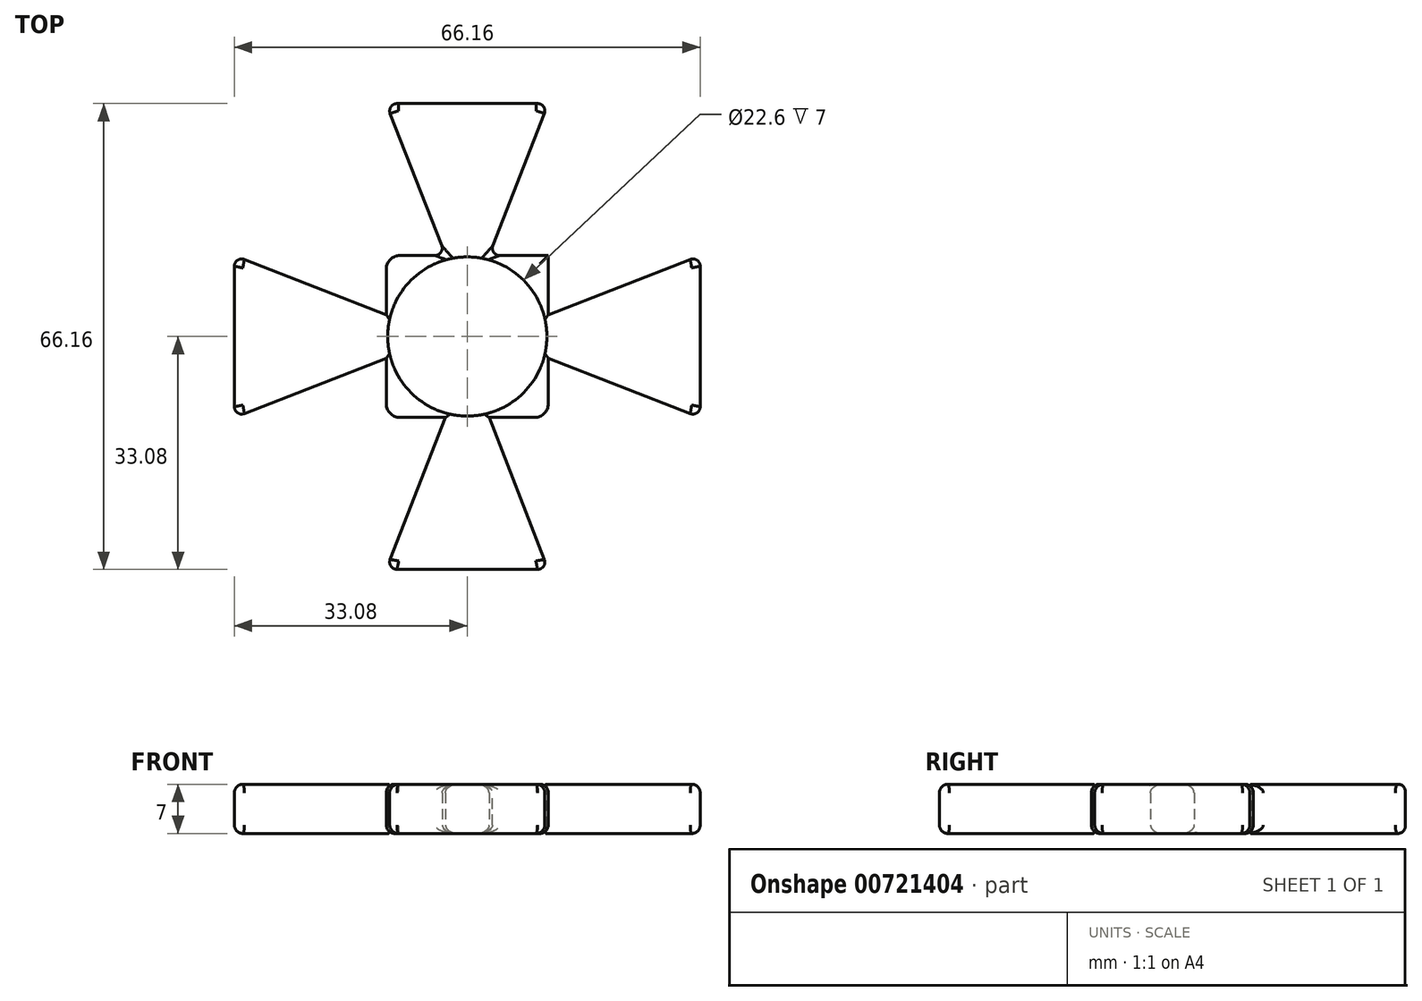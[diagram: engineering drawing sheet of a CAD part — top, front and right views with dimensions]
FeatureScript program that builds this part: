
annotation { "Feature Type Name" : "Feature", "Feature Type Description" : "" }
export const myFeature = defineFeature(function(context is Context, id is Id, definition is map)
    precondition{}
    {
        {
            var Q0;
            Q0=qCreatedBy(makeId("Top.planeOp"),FACE);
            var sketch = newSketch(context, id + "F0", { "sketchPlane" : qUnion([Q0])});
            skCircle(sketch, "E0", {"center": v(0, 0) * mm, "radius": 11.3 * mm});
            skLineSegment(sketch, "E1.bottom", {"start": v(11.5, 11.5) * mm, "end": v(-11.5, 11.5) * mm});
            skLineSegment(sketch, "E1.top", {"start": v(11.5, -11.5) * mm, "end": v(-11.5, -11.5) * mm});
            skLineSegment(sketch, "E1.left", {"start": v(11.5, 11.5) * mm, "end": v(11.5, -11.5) * mm});
            skLineSegment(sketch, "E1.right", {"start": v(-11.5, 11.5) * mm, "end": v(-11.5, -11.5) * mm});
            skLineSegment(sketch, "E2", {"start": v(-3.1, 11.5) * mm, "end": v(-11.5, 33.08) * mm});
            skLineSegment(sketch, "E3.MirrorCS", {"start": v(3.1, 11.5) * mm, "end": v(11.5, 33.08) * mm});
            skLineSegment(sketch, "E4", {"start": v(-11.5, 33.08) * mm, "end": v(11.5, 33.08) * mm});
            skLineSegment(sketch, "E5.MirrorCS", {"start": v(11.5, 33.08) * mm, "end": v(-11.5, 33.08) * mm});
            skLineSegment(sketch, "E6.MirrorCS", {"start": v(-3.1, -11.5) * mm, "end": v(-11.5, -33.08) * mm});
            skLineSegment(sketch, "E7.MirrorCS", {"start": v(3.1, -11.5) * mm, "end": v(11.5, -33.08) * mm});
            skLineSegment(sketch, "E8.MirrorCS", {"start": v(11.5, -33.08) * mm, "end": v(-11.5, -33.08) * mm});
            skLineSegment(sketch, "E9.MirrorCS", {"start": v(-11.5, 3.1) * mm, "end": v(-33.08, 11.5) * mm});
            skLineSegment(sketch, "E10.MirrorCS", {"start": v(-11.5, -3.1) * mm, "end": v(-33.08, -11.5) * mm});
            skLineSegment(sketch, "E11.MirrorCS", {"start": v(-33.08, -11.5) * mm, "end": v(-33.08, 11.5) * mm});
            skLineSegment(sketch, "E12.MirrorCS", {"start": v(11.5, 3.1) * mm, "end": v(33.08, 11.5) * mm});
            skLineSegment(sketch, "E13.MirrorCS", {"start": v(11.5, -3.1) * mm, "end": v(33.08, -11.5) * mm});
            skLineSegment(sketch, "E14.MirrorCS", {"start": v(33.08, -11.5) * mm, "end": v(33.08, 11.5) * mm});
            skSolve(sketch);
        }
        {
            var Q0;
            {var subQ0=sQuery(id+"F0.wireOp",EDGE,"E2");Q0=makeQuery(id+"F0.imprint","IMPRINT",FACE,{"disambiguationData":[TD([[makeQuery(id+"F0.imprint","IMPRINT",EDGE,{"derivedFrom":subQ0}),-1.0]])]});}
            var Q1;
            Q1=makeQuery(id+"F0.imprint","IMPRINT",FACE,{"disambiguationData":[TD([[makeQuery(id+"F0.imprint","IMPRINT",EDGE,{"derivedFrom":sQuery(id+"F0.wireOp",EDGE,"E0")}),-1.0]])]});
            var Q2;
            {var subQ0=sQuery(id+"F0.wireOp",EDGE,"E9.MirrorCS");Q2=makeQuery(id+"F0.imprint","IMPRINT",FACE,{"disambiguationData":[TD([[makeQuery(id+"F0.imprint","IMPRINT",EDGE,{"derivedFrom":subQ0}),1.0]])]});}
            var Q3;
            {var subQ0=sQuery(id+"F0.wireOp",EDGE,"E3.MirrorCS");Q3=makeQuery(id+"F0.imprint","IMPRINT",FACE,{"disambiguationData":[TD([[makeQuery(id+"F0.imprint","IMPRINT",EDGE,{"derivedFrom":subQ0}),1.0]])]});}
            var Q4;
            {var subQ0=sQuery(id+"F0.wireOp",EDGE,"E6.MirrorCS");Q4=makeQuery(id+"F0.imprint","IMPRINT",FACE,{"disambiguationData":[TD([[makeQuery(id+"F0.imprint","IMPRINT",EDGE,{"derivedFrom":subQ0}),1.0]])]});}
            var Q5;
            {var subQ0=sQuery(id+"F0.wireOp",EDGE,"E12.MirrorCS");Q5=makeQuery(id+"F0.imprint","IMPRINT",FACE,{"disambiguationData":[TD([[makeQuery(id+"F0.imprint","IMPRINT",EDGE,{"derivedFrom":subQ0}),-1.0]])]});}
            extrude(context, id + "F1", {"entities" : qUnion([Q0, Q1, Q2, Q3, Q4, Q5]), "depth" : 7 * mm, "offsetDistance" : 25 * mm});
        }
        {
            var Q0;
            Q0=makeQuery(id+"F1.opExtrude","SWEPT_EDGE",EDGE,{"disambiguationData":[OSD([sQuery(id+"F0.wireOp",EDGE,"E1.bottom"),sQuery(id+"F0.wireOp",EDGE,"E1.right")])]});
            var Q1;
            Q1=makeQuery(id+"F1.opExtrude","SWEPT_EDGE",EDGE,{"disambiguationData":[OSD([sQuery(id+"F0.wireOp",EDGE,"E1.top"),sQuery(id+"F0.wireOp",EDGE,"E1.left")])]});
            var Q2;
            Q2=makeQuery(id+"F1.opExtrude","SWEPT_EDGE",EDGE,{"disambiguationData":[OSD([sQuery(id+"F0.wireOp",EDGE,"E1.top"),sQuery(id+"F0.wireOp",EDGE,"E1.right")])]});
            fillet(context, id + "F2", {"entities" : qUnion([Q0, Q1, Q2]), "radius" : 1.93 * mm, "tangentPropagation" : true, "allowEdgeOverflow" : false});
        }
        {
            var Q0;
            {var subQ0=sQuery(id+"F0.wireOp",EDGE,"E1.right");Q0=makeQuery(id+"F1.opExtrude","CAP_EDGE",EDGE,{"disambiguationData":[OSD([subQ0]),TDD([makeQuery(id+"F0.imprint","IMPRINT",EDGE,{"disambiguationData":[TD([[makeQuery(id+"F0.imprint","INTERSECT",VERTEX,{"derivedFrom":[sQuery(id+"F0.wireOp",EDGE,"E1.bottom"),subQ0]}),-1.0]])],"derivedFrom":subQ0})])],"isStart":false});}
            var Q1;
            {var subQ0=sQuery(id+"F0.wireOp",EDGE,"E1.bottom");Q1=makeQuery(id+"F1.opExtrude","CAP_EDGE",EDGE,{"disambiguationData":[OSD([subQ0]),TDD([makeQuery(id+"F0.imprint","IMPRINT",EDGE,{"disambiguationData":[TD([[makeQuery(id+"F0.imprint","INTERSECT",VERTEX,{"derivedFrom":[subQ0,sQuery(id+"F0.wireOp",EDGE,"E1.right")]}),1.0]])],"derivedFrom":subQ0})])],"isStart":false});}
            var Q2;
            {var subQ0=sQuery(id+"F0.wireOp",EDGE,"E1.bottom");Q2=makeQuery(id+"F1.opExtrude","CAP_EDGE",EDGE,{"disambiguationData":[OSD([subQ0]),TDD([makeQuery(id+"F0.imprint","IMPRINT",EDGE,{"disambiguationData":[TD([[makeQuery(id+"F0.imprint","INTERSECT",VERTEX,{"derivedFrom":[subQ0,sQuery(id+"F0.wireOp",EDGE,"E1.left")]}),-1.0]])],"derivedFrom":subQ0})])],"isStart":false});}
            var Q3;
            {var subQ0=sQuery(id+"F0.wireOp",EDGE,"E1.left");Q3=makeQuery(id+"F1.opExtrude","CAP_EDGE",EDGE,{"disambiguationData":[OSD([subQ0]),TDD([makeQuery(id+"F0.imprint","IMPRINT",EDGE,{"disambiguationData":[TD([[makeQuery(id+"F0.imprint","INTERSECT",VERTEX,{"derivedFrom":[sQuery(id+"F0.wireOp",EDGE,"E1.bottom"),subQ0]}),-1.0]])],"derivedFrom":subQ0})])],"isStart":false});}
            var Q4;
            {var subQ0=sQuery(id+"F0.wireOp",EDGE,"E1.left");Q4=makeQuery(id+"F1.opExtrude","CAP_EDGE",EDGE,{"disambiguationData":[OSD([subQ0]),TDD([makeQuery(id+"F0.imprint","IMPRINT",EDGE,{"disambiguationData":[TD([[makeQuery(id+"F0.imprint","INTERSECT",VERTEX,{"derivedFrom":[sQuery(id+"F0.wireOp",EDGE,"E1.top"),subQ0]}),1.0]])],"derivedFrom":subQ0})])],"isStart":false});}
            var Q5;
            {var subQ0=sQuery(id+"F0.wireOp",EDGE,"E1.top");Q5=makeQuery(id+"F1.opExtrude","CAP_EDGE",EDGE,{"disambiguationData":[OSD([subQ0]),TDD([makeQuery(id+"F0.imprint","IMPRINT",EDGE,{"disambiguationData":[TD([[makeQuery(id+"F0.imprint","INTERSECT",VERTEX,{"derivedFrom":[subQ0,sQuery(id+"F0.wireOp",EDGE,"E1.left")]}),-1.0]])],"derivedFrom":subQ0})])],"isStart":false});}
            var Q6;
            {var subQ0=sQuery(id+"F0.wireOp",EDGE,"E1.left");var subQ1=sQuery(id+"F0.wireOp",EDGE,"E1.top");Q6=makeQuery(id+"F2.opFillet","BLEND_EDGE",EDGE,{"blendedFrom":[makeQuery(id+"F1.opExtrude","SWEPT_EDGE",EDGE,{"disambiguationData":[OSD([subQ1,subQ0])]}),makeQuery(id+"F1.opExtrude","CAP_FACE",FACE,{"disambiguationData":[OSD([sQuery(id+"F0.wireOp",EDGE,"E0"),sQuery(id+"F0.wireOp",EDGE,"E1.bottom"),subQ1,subQ0,sQuery(id+"F0.wireOp",EDGE,"E1.right"),sQuery(id+"F0.wireOp",EDGE,"E3.MirrorCS"),sQuery(id+"F0.wireOp",EDGE,"E2"),sQuery(id+"F0.wireOp",EDGE,"E5.MirrorCS"),sQuery(id+"F0.wireOp",EDGE,"E6.MirrorCS"),sQuery(id+"F0.wireOp",EDGE,"E7.MirrorCS"),sQuery(id+"F0.wireOp",EDGE,"E8.MirrorCS"),sQuery(id+"F0.wireOp",EDGE,"E9.MirrorCS"),sQuery(id+"F0.wireOp",EDGE,"E10.MirrorCS"),sQuery(id+"F0.wireOp",EDGE,"E11.MirrorCS"),sQuery(id+"F0.wireOp",EDGE,"E12.MirrorCS"),sQuery(id+"F0.wireOp",EDGE,"E13.MirrorCS"),sQuery(id+"F0.wireOp",EDGE,"E14.MirrorCS")])],"isStart":false})],"blendedInto":[makeQuery(id+"F1.opExtrude","CAP_FACE",FACE,{"disambiguationData":[OSD([sQuery(id+"F0.wireOp",EDGE,"E0"),sQuery(id+"F0.wireOp",EDGE,"E1.bottom"),subQ1,subQ0,sQuery(id+"F0.wireOp",EDGE,"E1.right"),sQuery(id+"F0.wireOp",EDGE,"E3.MirrorCS"),sQuery(id+"F0.wireOp",EDGE,"E2"),sQuery(id+"F0.wireOp",EDGE,"E5.MirrorCS"),sQuery(id+"F0.wireOp",EDGE,"E6.MirrorCS"),sQuery(id+"F0.wireOp",EDGE,"E7.MirrorCS"),sQuery(id+"F0.wireOp",EDGE,"E8.MirrorCS"),sQuery(id+"F0.wireOp",EDGE,"E9.MirrorCS"),sQuery(id+"F0.wireOp",EDGE,"E10.MirrorCS"),sQuery(id+"F0.wireOp",EDGE,"E11.MirrorCS"),sQuery(id+"F0.wireOp",EDGE,"E12.MirrorCS"),sQuery(id+"F0.wireOp",EDGE,"E13.MirrorCS"),sQuery(id+"F0.wireOp",EDGE,"E14.MirrorCS")])],"isStart":false})]});}
            var Q7;
            {var subQ0=sQuery(id+"F0.wireOp",EDGE,"E1.top");Q7=makeQuery(id+"F1.opExtrude","CAP_EDGE",EDGE,{"disambiguationData":[OSD([subQ0]),TDD([makeQuery(id+"F0.imprint","IMPRINT",EDGE,{"disambiguationData":[TD([[makeQuery(id+"F0.imprint","INTERSECT",VERTEX,{"derivedFrom":[subQ0,sQuery(id+"F0.wireOp",EDGE,"E1.right")]}),1.0]])],"derivedFrom":subQ0})])],"isStart":false});}
            var Q8;
            {var subQ0=sQuery(id+"F0.wireOp",EDGE,"E1.right");var subQ1=sQuery(id+"F0.wireOp",EDGE,"E1.top");Q8=makeQuery(id+"F2.opFillet","BLEND_EDGE",EDGE,{"blendedFrom":[makeQuery(id+"F1.opExtrude","SWEPT_EDGE",EDGE,{"disambiguationData":[OSD([subQ1,subQ0])]}),makeQuery(id+"F1.opExtrude","CAP_FACE",FACE,{"disambiguationData":[OSD([sQuery(id+"F0.wireOp",EDGE,"E0"),sQuery(id+"F0.wireOp",EDGE,"E1.bottom"),subQ1,sQuery(id+"F0.wireOp",EDGE,"E1.left"),subQ0,sQuery(id+"F0.wireOp",EDGE,"E3.MirrorCS"),sQuery(id+"F0.wireOp",EDGE,"E2"),sQuery(id+"F0.wireOp",EDGE,"E5.MirrorCS"),sQuery(id+"F0.wireOp",EDGE,"E6.MirrorCS"),sQuery(id+"F0.wireOp",EDGE,"E7.MirrorCS"),sQuery(id+"F0.wireOp",EDGE,"E8.MirrorCS"),sQuery(id+"F0.wireOp",EDGE,"E9.MirrorCS"),sQuery(id+"F0.wireOp",EDGE,"E10.MirrorCS"),sQuery(id+"F0.wireOp",EDGE,"E11.MirrorCS"),sQuery(id+"F0.wireOp",EDGE,"E12.MirrorCS"),sQuery(id+"F0.wireOp",EDGE,"E13.MirrorCS"),sQuery(id+"F0.wireOp",EDGE,"E14.MirrorCS")])],"isStart":false})],"blendedInto":[makeQuery(id+"F1.opExtrude","CAP_FACE",FACE,{"disambiguationData":[OSD([sQuery(id+"F0.wireOp",EDGE,"E0"),sQuery(id+"F0.wireOp",EDGE,"E1.bottom"),subQ1,sQuery(id+"F0.wireOp",EDGE,"E1.left"),subQ0,sQuery(id+"F0.wireOp",EDGE,"E3.MirrorCS"),sQuery(id+"F0.wireOp",EDGE,"E2"),sQuery(id+"F0.wireOp",EDGE,"E5.MirrorCS"),sQuery(id+"F0.wireOp",EDGE,"E6.MirrorCS"),sQuery(id+"F0.wireOp",EDGE,"E7.MirrorCS"),sQuery(id+"F0.wireOp",EDGE,"E8.MirrorCS"),sQuery(id+"F0.wireOp",EDGE,"E9.MirrorCS"),sQuery(id+"F0.wireOp",EDGE,"E10.MirrorCS"),sQuery(id+"F0.wireOp",EDGE,"E11.MirrorCS"),sQuery(id+"F0.wireOp",EDGE,"E12.MirrorCS"),sQuery(id+"F0.wireOp",EDGE,"E13.MirrorCS"),sQuery(id+"F0.wireOp",EDGE,"E14.MirrorCS")])],"isStart":false})]});}
            var Q9;
            {var subQ0=sQuery(id+"F0.wireOp",EDGE,"E1.right");Q9=makeQuery(id+"F1.opExtrude","CAP_EDGE",EDGE,{"disambiguationData":[OSD([subQ0]),TDD([makeQuery(id+"F0.imprint","IMPRINT",EDGE,{"disambiguationData":[TD([[makeQuery(id+"F0.imprint","INTERSECT",VERTEX,{"derivedFrom":[sQuery(id+"F0.wireOp",EDGE,"E1.top"),subQ0]}),1.0]])],"derivedFrom":subQ0})])],"isStart":false});}
            var Q10;
            {var subQ0=sQuery(id+"F0.wireOp",EDGE,"E1.right");var subQ1=sQuery(id+"F0.wireOp",EDGE,"E1.bottom");Q10=makeQuery(id+"F2.opFillet","BLEND_EDGE",EDGE,{"blendedFrom":[makeQuery(id+"F1.opExtrude","SWEPT_EDGE",EDGE,{"disambiguationData":[OSD([subQ1,subQ0])]}),makeQuery(id+"F1.opExtrude","CAP_FACE",FACE,{"disambiguationData":[OSD([sQuery(id+"F0.wireOp",EDGE,"E0"),subQ1,sQuery(id+"F0.wireOp",EDGE,"E1.top"),sQuery(id+"F0.wireOp",EDGE,"E1.left"),subQ0,sQuery(id+"F0.wireOp",EDGE,"E3.MirrorCS"),sQuery(id+"F0.wireOp",EDGE,"E2"),sQuery(id+"F0.wireOp",EDGE,"E5.MirrorCS"),sQuery(id+"F0.wireOp",EDGE,"E6.MirrorCS"),sQuery(id+"F0.wireOp",EDGE,"E7.MirrorCS"),sQuery(id+"F0.wireOp",EDGE,"E8.MirrorCS"),sQuery(id+"F0.wireOp",EDGE,"E9.MirrorCS"),sQuery(id+"F0.wireOp",EDGE,"E10.MirrorCS"),sQuery(id+"F0.wireOp",EDGE,"E11.MirrorCS"),sQuery(id+"F0.wireOp",EDGE,"E12.MirrorCS"),sQuery(id+"F0.wireOp",EDGE,"E13.MirrorCS"),sQuery(id+"F0.wireOp",EDGE,"E14.MirrorCS")])],"isStart":false})],"blendedInto":[makeQuery(id+"F1.opExtrude","CAP_FACE",FACE,{"disambiguationData":[OSD([sQuery(id+"F0.wireOp",EDGE,"E0"),subQ1,sQuery(id+"F0.wireOp",EDGE,"E1.top"),sQuery(id+"F0.wireOp",EDGE,"E1.left"),subQ0,sQuery(id+"F0.wireOp",EDGE,"E3.MirrorCS"),sQuery(id+"F0.wireOp",EDGE,"E2"),sQuery(id+"F0.wireOp",EDGE,"E5.MirrorCS"),sQuery(id+"F0.wireOp",EDGE,"E6.MirrorCS"),sQuery(id+"F0.wireOp",EDGE,"E7.MirrorCS"),sQuery(id+"F0.wireOp",EDGE,"E8.MirrorCS"),sQuery(id+"F0.wireOp",EDGE,"E9.MirrorCS"),sQuery(id+"F0.wireOp",EDGE,"E10.MirrorCS"),sQuery(id+"F0.wireOp",EDGE,"E11.MirrorCS"),sQuery(id+"F0.wireOp",EDGE,"E12.MirrorCS"),sQuery(id+"F0.wireOp",EDGE,"E13.MirrorCS"),sQuery(id+"F0.wireOp",EDGE,"E14.MirrorCS")])],"isStart":false})]});}
            var Q11;
            Q11=makeQuery(id+"F1.opExtrude","CAP_EDGE",EDGE,{"disambiguationData":[OSD([sQuery(id+"F0.wireOp",EDGE,"E13.MirrorCS")])],"isStart":false});
            var Q12;
            Q12=makeQuery(id+"F1.opExtrude","CAP_EDGE",EDGE,{"disambiguationData":[OSD([sQuery(id+"F0.wireOp",EDGE,"E12.MirrorCS")])],"isStart":false});
            var Q13;
            Q13=makeQuery(id+"F1.opExtrude","CAP_EDGE",EDGE,{"disambiguationData":[OSD([sQuery(id+"F0.wireOp",EDGE,"E14.MirrorCS")])],"isStart":false});
            var Q14;
            Q14=makeQuery(id+"F1.opExtrude","CAP_EDGE",EDGE,{"disambiguationData":[OSD([sQuery(id+"F0.wireOp",EDGE,"E10.MirrorCS")])],"isStart":false});
            var Q15;
            Q15=makeQuery(id+"F1.opExtrude","CAP_EDGE",EDGE,{"disambiguationData":[OSD([sQuery(id+"F0.wireOp",EDGE,"E9.MirrorCS")])],"isStart":false});
            var Q16;
            Q16=makeQuery(id+"F1.opExtrude","CAP_EDGE",EDGE,{"disambiguationData":[OSD([sQuery(id+"F0.wireOp",EDGE,"E11.MirrorCS")])],"isStart":false});
            var Q17;
            Q17=makeQuery(id+"F1.opExtrude","CAP_EDGE",EDGE,{"disambiguationData":[OSD([sQuery(id+"F0.wireOp",EDGE,"E3.MirrorCS")])],"isStart":false});
            var Q18;
            Q18=makeQuery(id+"F1.opExtrude","CAP_EDGE",EDGE,{"disambiguationData":[OSD([sQuery(id+"F0.wireOp",EDGE,"E2")])],"isStart":false});
            var Q19;
            Q19=makeQuery(id+"F1.opExtrude","CAP_EDGE",EDGE,{"disambiguationData":[OSD([sQuery(id+"F0.wireOp",EDGE,"E7.MirrorCS")])],"isStart":false});
            var Q20;
            Q20=makeQuery(id+"F1.opExtrude","CAP_EDGE",EDGE,{"disambiguationData":[OSD([sQuery(id+"F0.wireOp",EDGE,"E6.MirrorCS")])],"isStart":false});
            var Q21;
            Q21=makeQuery(id+"F1.opExtrude","CAP_EDGE",EDGE,{"disambiguationData":[OSD([sQuery(id+"F0.wireOp",EDGE,"E8.MirrorCS")])],"isStart":false});
            var Q22;
            Q22=makeQuery(id+"F1.opExtrude","CAP_EDGE",EDGE,{"disambiguationData":[OSD([sQuery(id+"F0.wireOp",EDGE,"E5.MirrorCS")])],"isStart":false});
            var Q23;
            {var subQ0=sQuery(id+"F0.wireOp",EDGE,"E1.top");Q23=makeQuery(id+"F1.opExtrude","CAP_EDGE",EDGE,{"disambiguationData":[OSD([subQ0]),TDD([makeQuery(id+"F0.imprint","IMPRINT",EDGE,{"disambiguationData":[TD([[makeQuery(id+"F0.imprint","INTERSECT",VERTEX,{"derivedFrom":[subQ0,sQuery(id+"F0.wireOp",EDGE,"E1.right")]}),1.0]])],"derivedFrom":subQ0})])],"isStart":true});}
            var Q24;
            {var subQ0=sQuery(id+"F0.wireOp",EDGE,"E1.right");Q24=makeQuery(id+"F1.opExtrude","CAP_EDGE",EDGE,{"disambiguationData":[OSD([subQ0]),TDD([makeQuery(id+"F0.imprint","IMPRINT",EDGE,{"disambiguationData":[TD([[makeQuery(id+"F0.imprint","INTERSECT",VERTEX,{"derivedFrom":[sQuery(id+"F0.wireOp",EDGE,"E1.top"),subQ0]}),1.0]])],"derivedFrom":subQ0})])],"isStart":true});}
            var Q25;
            Q25=makeQuery(id+"F1.opExtrude","CAP_EDGE",EDGE,{"disambiguationData":[OSD([sQuery(id+"F0.wireOp",EDGE,"E10.MirrorCS")])],"isStart":true});
            var Q26;
            Q26=makeQuery(id+"F1.opExtrude","CAP_EDGE",EDGE,{"disambiguationData":[OSD([sQuery(id+"F0.wireOp",EDGE,"E11.MirrorCS")])],"isStart":true});
            var Q27;
            Q27=makeQuery(id+"F1.opExtrude","CAP_EDGE",EDGE,{"disambiguationData":[OSD([sQuery(id+"F0.wireOp",EDGE,"E9.MirrorCS")])],"isStart":true});
            var Q28;
            {var subQ0=sQuery(id+"F0.wireOp",EDGE,"E1.right");Q28=makeQuery(id+"F1.opExtrude","CAP_EDGE",EDGE,{"disambiguationData":[OSD([subQ0]),TDD([makeQuery(id+"F0.imprint","IMPRINT",EDGE,{"disambiguationData":[TD([[makeQuery(id+"F0.imprint","INTERSECT",VERTEX,{"derivedFrom":[sQuery(id+"F0.wireOp",EDGE,"E1.bottom"),subQ0]}),-1.0]])],"derivedFrom":subQ0})])],"isStart":true});}
            var Q29;
            Q29=makeQuery(id+"F1.opExtrude","CAP_EDGE",EDGE,{"disambiguationData":[OSD([sQuery(id+"F0.wireOp",EDGE,"E2")])],"isStart":true});
            var Q30;
            Q30=makeQuery(id+"F1.opExtrude","CAP_EDGE",EDGE,{"disambiguationData":[OSD([sQuery(id+"F0.wireOp",EDGE,"E3.MirrorCS")])],"isStart":true});
            var Q31;
            {var subQ0=sQuery(id+"F0.wireOp",EDGE,"E1.bottom");Q31=makeQuery(id+"F1.opExtrude","CAP_EDGE",EDGE,{"disambiguationData":[OSD([subQ0]),TDD([makeQuery(id+"F0.imprint","IMPRINT",EDGE,{"disambiguationData":[TD([[makeQuery(id+"F0.imprint","INTERSECT",VERTEX,{"derivedFrom":[subQ0,sQuery(id+"F0.wireOp",EDGE,"E1.left")]}),-1.0]])],"derivedFrom":subQ0})])],"isStart":true});}
            var Q32;
            {var subQ0=sQuery(id+"F0.wireOp",EDGE,"E1.left");Q32=makeQuery(id+"F1.opExtrude","CAP_EDGE",EDGE,{"disambiguationData":[OSD([subQ0]),TDD([makeQuery(id+"F0.imprint","IMPRINT",EDGE,{"disambiguationData":[TD([[makeQuery(id+"F0.imprint","INTERSECT",VERTEX,{"derivedFrom":[sQuery(id+"F0.wireOp",EDGE,"E1.bottom"),subQ0]}),-1.0]])],"derivedFrom":subQ0})])],"isStart":true});}
            var Q33;
            Q33=makeQuery(id+"F1.opExtrude","CAP_EDGE",EDGE,{"disambiguationData":[OSD([sQuery(id+"F0.wireOp",EDGE,"E12.MirrorCS")])],"isStart":true});
            var Q34;
            Q34=makeQuery(id+"F1.opExtrude","CAP_EDGE",EDGE,{"disambiguationData":[OSD([sQuery(id+"F0.wireOp",EDGE,"E13.MirrorCS")])],"isStart":true});
            var Q35;
            {var subQ0=sQuery(id+"F0.wireOp",EDGE,"E1.left");var subQ1=sQuery(id+"F0.wireOp",EDGE,"E1.top");Q35=makeQuery(id+"F2.opFillet","BLEND_EDGE",EDGE,{"blendedFrom":[makeQuery(id+"F1.opExtrude","SWEPT_EDGE",EDGE,{"disambiguationData":[OSD([subQ1,subQ0])]}),makeQuery(id+"F1.opExtrude","CAP_FACE",FACE,{"disambiguationData":[OSD([sQuery(id+"F0.wireOp",EDGE,"E0"),sQuery(id+"F0.wireOp",EDGE,"E1.bottom"),subQ1,subQ0,sQuery(id+"F0.wireOp",EDGE,"E1.right"),sQuery(id+"F0.wireOp",EDGE,"E3.MirrorCS"),sQuery(id+"F0.wireOp",EDGE,"E2"),sQuery(id+"F0.wireOp",EDGE,"E5.MirrorCS"),sQuery(id+"F0.wireOp",EDGE,"E6.MirrorCS"),sQuery(id+"F0.wireOp",EDGE,"E7.MirrorCS"),sQuery(id+"F0.wireOp",EDGE,"E8.MirrorCS"),sQuery(id+"F0.wireOp",EDGE,"E9.MirrorCS"),sQuery(id+"F0.wireOp",EDGE,"E10.MirrorCS"),sQuery(id+"F0.wireOp",EDGE,"E11.MirrorCS"),sQuery(id+"F0.wireOp",EDGE,"E12.MirrorCS"),sQuery(id+"F0.wireOp",EDGE,"E13.MirrorCS"),sQuery(id+"F0.wireOp",EDGE,"E14.MirrorCS")])],"isStart":true})],"blendedInto":[makeQuery(id+"F1.opExtrude","CAP_FACE",FACE,{"disambiguationData":[OSD([sQuery(id+"F0.wireOp",EDGE,"E0"),sQuery(id+"F0.wireOp",EDGE,"E1.bottom"),subQ1,subQ0,sQuery(id+"F0.wireOp",EDGE,"E1.right"),sQuery(id+"F0.wireOp",EDGE,"E3.MirrorCS"),sQuery(id+"F0.wireOp",EDGE,"E2"),sQuery(id+"F0.wireOp",EDGE,"E5.MirrorCS"),sQuery(id+"F0.wireOp",EDGE,"E6.MirrorCS"),sQuery(id+"F0.wireOp",EDGE,"E7.MirrorCS"),sQuery(id+"F0.wireOp",EDGE,"E8.MirrorCS"),sQuery(id+"F0.wireOp",EDGE,"E9.MirrorCS"),sQuery(id+"F0.wireOp",EDGE,"E10.MirrorCS"),sQuery(id+"F0.wireOp",EDGE,"E11.MirrorCS"),sQuery(id+"F0.wireOp",EDGE,"E12.MirrorCS"),sQuery(id+"F0.wireOp",EDGE,"E13.MirrorCS"),sQuery(id+"F0.wireOp",EDGE,"E14.MirrorCS")])],"isStart":true})]});}
            var Q36;
            Q36=makeQuery(id+"F1.opExtrude","CAP_EDGE",EDGE,{"disambiguationData":[OSD([sQuery(id+"F0.wireOp",EDGE,"E7.MirrorCS")])],"isStart":true});
            var Q37;
            Q37=makeQuery(id+"F1.opExtrude","CAP_EDGE",EDGE,{"disambiguationData":[OSD([sQuery(id+"F0.wireOp",EDGE,"E6.MirrorCS")])],"isStart":true});
            var Q38;
            Q38=makeQuery(id+"F1.opExtrude","CAP_EDGE",EDGE,{"disambiguationData":[OSD([sQuery(id+"F0.wireOp",EDGE,"E5.MirrorCS")])],"isStart":true});
            var Q39;
            Q39=makeQuery(id+"F1.opExtrude","CAP_EDGE",EDGE,{"disambiguationData":[OSD([sQuery(id+"F0.wireOp",EDGE,"E14.MirrorCS")])],"isStart":true});
            var Q40;
            Q40=makeQuery(id+"F1.opExtrude","CAP_EDGE",EDGE,{"disambiguationData":[OSD([sQuery(id+"F0.wireOp",EDGE,"E8.MirrorCS")])],"isStart":true});
            fillet(context, id + "F3", {"entities" : qUnion([Q0, Q1, Q2, Q3, Q4, Q5, Q6, Q7, Q8, Q9, Q10, Q11, Q12, Q13, Q14, Q15, Q16, Q17, Q18, Q19, Q20, Q21, Q22, Q23, Q24, Q25, Q26, Q27, Q28, Q29, Q30, Q31, Q32, Q33, Q34, Q35, Q36, Q37, Q38, Q39, Q40]), "radius" : 1.2 * mm, "tangentPropagation" : true, "allowEdgeOverflow" : false});
        }
        {
            var Q0;
            Q0=makeQuery(id+"F1.opExtrude","SWEPT_EDGE",EDGE,{"disambiguationData":[OSD([sQuery(id+"F0.wireOp",EDGE,"E12.MirrorCS"),sQuery(id+"F0.wireOp",EDGE,"E14.MirrorCS")])]});
            var Q1;
            Q1=makeQuery(id+"F1.opExtrude","SWEPT_EDGE",EDGE,{"disambiguationData":[OSD([sQuery(id+"F0.wireOp",EDGE,"E13.MirrorCS"),sQuery(id+"F0.wireOp",EDGE,"E14.MirrorCS")])]});
            var Q2;
            Q2=makeQuery(id+"F1.opExtrude","SWEPT_EDGE",EDGE,{"disambiguationData":[OSD([sQuery(id+"F0.wireOp",EDGE,"E7.MirrorCS"),sQuery(id+"F0.wireOp",EDGE,"E8.MirrorCS")])]});
            var Q3;
            Q3=makeQuery(id+"F1.opExtrude","SWEPT_EDGE",EDGE,{"disambiguationData":[OSD([sQuery(id+"F0.wireOp",EDGE,"E6.MirrorCS"),sQuery(id+"F0.wireOp",EDGE,"E8.MirrorCS")])]});
            var Q4;
            Q4=makeQuery(id+"F1.opExtrude","SWEPT_EDGE",EDGE,{"disambiguationData":[OSD([sQuery(id+"F0.wireOp",EDGE,"E10.MirrorCS"),sQuery(id+"F0.wireOp",EDGE,"E11.MirrorCS")])]});
            var Q5;
            Q5=makeQuery(id+"F1.opExtrude","SWEPT_EDGE",EDGE,{"disambiguationData":[OSD([sQuery(id+"F0.wireOp",EDGE,"E9.MirrorCS"),sQuery(id+"F0.wireOp",EDGE,"E11.MirrorCS")])]});
            var Q6;
            Q6=makeQuery(id+"F1.opExtrude","SWEPT_EDGE",EDGE,{"disambiguationData":[OSD([sQuery(id+"F0.wireOp",EDGE,"E2"),sQuery(id+"F0.wireOp",EDGE,"E5.MirrorCS")])]});
            var Q7;
            Q7=makeQuery(id+"F1.opExtrude","SWEPT_EDGE",EDGE,{"disambiguationData":[OSD([sQuery(id+"F0.wireOp",EDGE,"E3.MirrorCS"),sQuery(id+"F0.wireOp",EDGE,"E5.MirrorCS")])]});
            fillet(context, id + "F4", {"entities" : qUnion([Q0, Q1, Q2, Q3, Q4, Q5, Q6, Q7]), "radius" : 1.04 * mm, "tangentPropagation" : true, "allowEdgeOverflow" : false});
        }
    });
